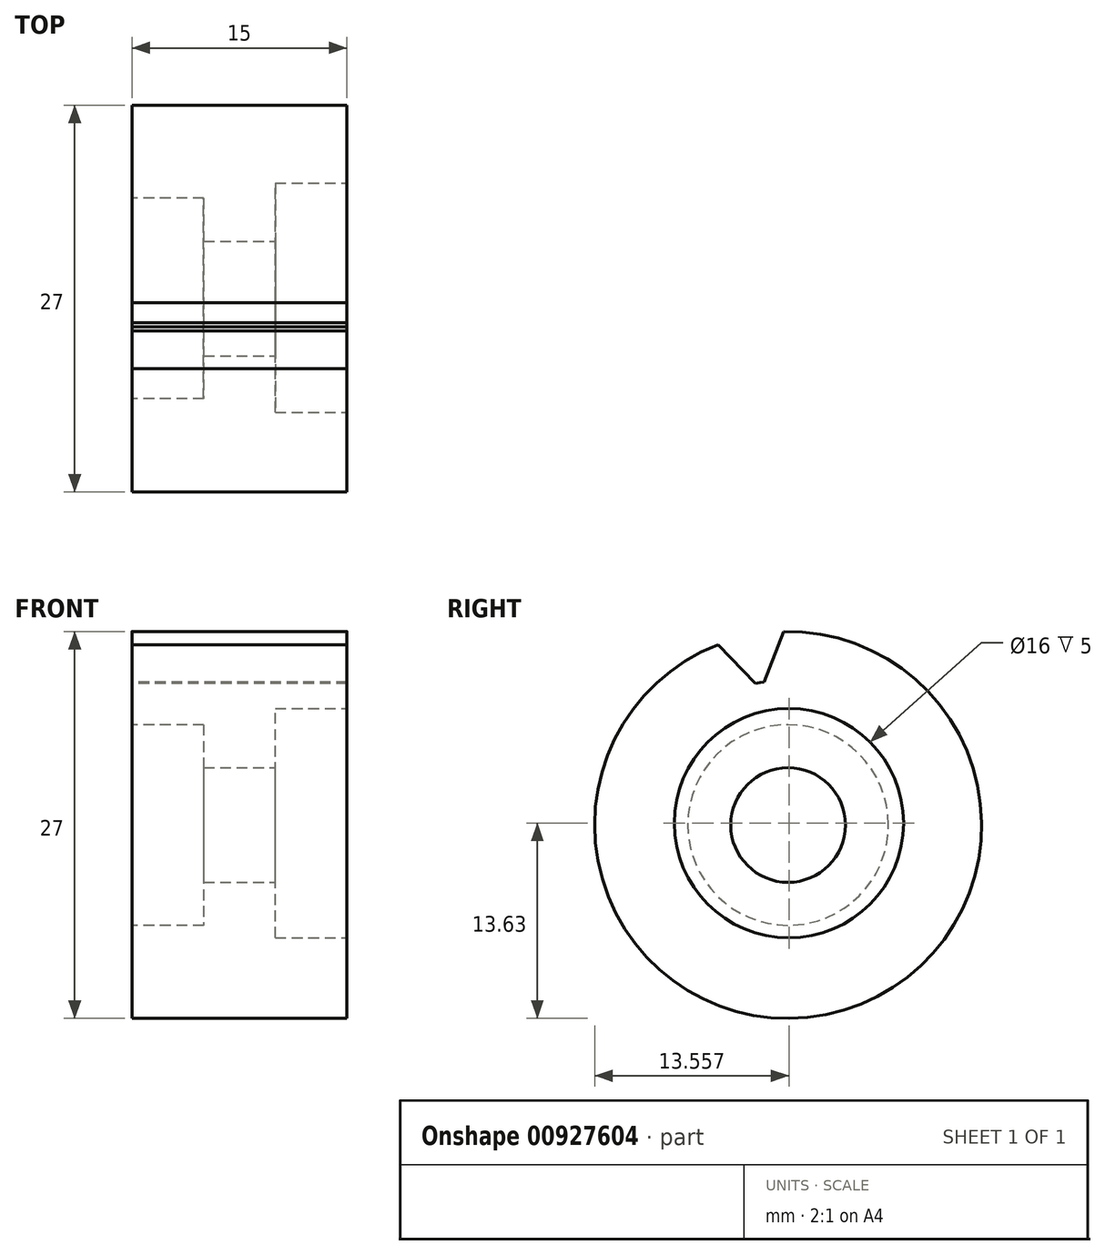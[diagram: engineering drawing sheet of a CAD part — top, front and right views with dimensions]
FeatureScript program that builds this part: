
annotation { "Feature Type Name" : "Feature", "Feature Type Description" : "" }
export const myFeature = defineFeature(function(context is Context, id is Id, definition is map)
    precondition{}
    {
        {
            var Q0;
            Q0=qCreatedBy(makeId("Right.planeOp"),FACE);
            var sketch = newSketch(context, id + "F0", { "sketchPlane" : qUnion([Q0])});
            skCircle(sketch, "E0", {"center": v(0, 0) * mm, "radius": 13.5 * mm});
            skSolve(sketch);
        }
        {
            var Q0;
            Q0=makeQuery(id+"F0.imprint","IMPRINT",FACE,{"disambiguationData":[TD([[makeQuery(id+"F0.imprint","IMPRINT",EDGE,{"derivedFrom":sQuery(id+"F0.wireOp",EDGE,"E0")}),1.0]])]});
            extrude(context, id + "F1", {"entities" : qUnion([Q0]), "oppositeDirection" : true, "depth" : 15 * mm, "offsetDistance" : 25 * mm});
        }
        {
            var Q0;
            Q0=makeQuery(id+"F1.opExtrude","CAP_FACE",FACE,{"disambiguationData":[OSD([sQuery(id+"F0.wireOp",EDGE,"E0")])],"isStart":false});
            var sketch = newSketch(context, id + "F2", { "sketchPlane" : qUnion([Q0])});
            skCircle(sketch, "E1", {"center": v(0, 0) * mm, "radius": 7 * mm});
            skSolve(sketch);
        }
        {
            var Q0;
            Q0 = qSketchRegion(id + "F2", true);
            extrude(context, id + "F3", {"entities" : qUnion([Q0]), "operationType" : NewBodyOperationType.REMOVE, "oppositeDirection" : true, "depth" : 5 * mm, "offsetDistance" : 25 * mm});
        }
        {
            var Q0;
            Q0=makeQuery(id+"F1.opExtrude","CAP_FACE",FACE,{"disambiguationData":[OSD([sQuery(id+"F0.wireOp",EDGE,"E0")])],"isStart":false});
            var sketch = newSketch(context, id + "F4", { "sketchPlane" : qUnion([Q0])});
            skLineSegment(sketch, "E2", {"start": v(0, 0) * mm, "end": v(0, 23.71) * mm, "construction": true});
            skLineSegment(sketch, "E3", {"start": v(0, 0) * mm, "end": v(9.4, 22.69) * mm, "construction": true});
            skLineSegment(sketch, "E4", {"start": v(0, 0) * mm, "end": v(4.64, 23.33) * mm, "construction": true});
            skCircle(sketch, "E5", {"center": v(0, 0) * mm, "radius": 10.12 * mm, "construction": true});
            skLineSegment(sketch, "E6", {"start": v(5.17, 12.47) * mm, "end": v(4.89, 12.58) * mm});
            skLineSegment(sketch, "E7", {"start": v(0, 13.5) * mm, "end": v(0.3, 13.5) * mm});
            skLineSegment(sketch, "E8", {"start": v(1.98, 9.93) * mm, "end": v(2.27, 9.87) * mm});
            skLineSegment(sketch, "E9.MirrorCS", {"start": v(1.98, 9.93) * mm, "end": v(1.68, 9.98) * mm});
            skLineSegment(sketch, "E10", {"start": v(4.89, 12.58) * mm, "end": v(2.27, 9.87) * mm});
            skLineSegment(sketch, "E11", {"start": v(0.3, 13.5) * mm, "end": v(1.68, 9.98) * mm});
            skSolve(sketch);
        }
        {
            var Q0;
            Q0=makeQuery(id+"F4.imprint","IMPRINT",FACE,{"disambiguationData":[TD([[makeQuery(id+"F4.imprint","IMPRINT",EDGE,{"derivedFrom":sQuery(id+"F4.wireOp",EDGE,"E8")}),1.0]])]});
            extrude(context, id + "F5", {"entities" : qUnion([Q0]), "operationType" : NewBodyOperationType.REMOVE, "endBound" : BoundingType.THROUGH_ALL, "oppositeDirection" : true, "depth" : 25 * mm, "offsetDistance" : 25 * mm});
        }
        {
            var Q0;
            Q0=makeQuery(id+"F1.opExtrude","CAP_FACE",FACE,{"disambiguationData":[OSD([sQuery(id+"F0.wireOp",EDGE,"E0")])],"isStart":true});
            var sketch = newSketch(context, id + "F6", { "sketchPlane" : qUnion([Q0])});
            skCircle(sketch, "E12", {"center": v(0.06, 0.13) * mm, "radius": 8 * mm});
            skSolve(sketch);
        }
        {
            var Q0;
            Q0 = qSketchRegion(id + "F6", true);
            extrude(context, id + "F7", {"entities" : qUnion([Q0]), "operationType" : NewBodyOperationType.REMOVE, "oppositeDirection" : true, "depth" : 5 * mm, "offsetDistance" : 25 * mm});
        }
        {
            var Q0;
            Q0=makeQuery(id+"F7.boolean.opBoolean","COPY",FACE,{"derivedFrom":makeQuery(id+"F7.opExtrude","CAP_FACE",FACE,{"disambiguationData":[OSD([sQuery(id+"F6.wireOp",EDGE,"E12")])],"isStart":false})});
            var sketch = newSketch(context, id + "F8", { "sketchPlane" : qUnion([Q0])});
            skCircle(sketch, "E13", {"center": v(0, 0) * mm, "radius": 4 * mm});
            skSolve(sketch);
        }
        {
            var Q0;
            Q0 = qSketchRegion(id + "F8", true);
            extrude(context, id + "F9", {"entities" : qUnion([Q0]), "operationType" : NewBodyOperationType.REMOVE, "endBound" : BoundingType.THROUGH_ALL, "oppositeDirection" : true, "depth" : 25 * mm, "offsetDistance" : 25 * mm});
        }
    });
